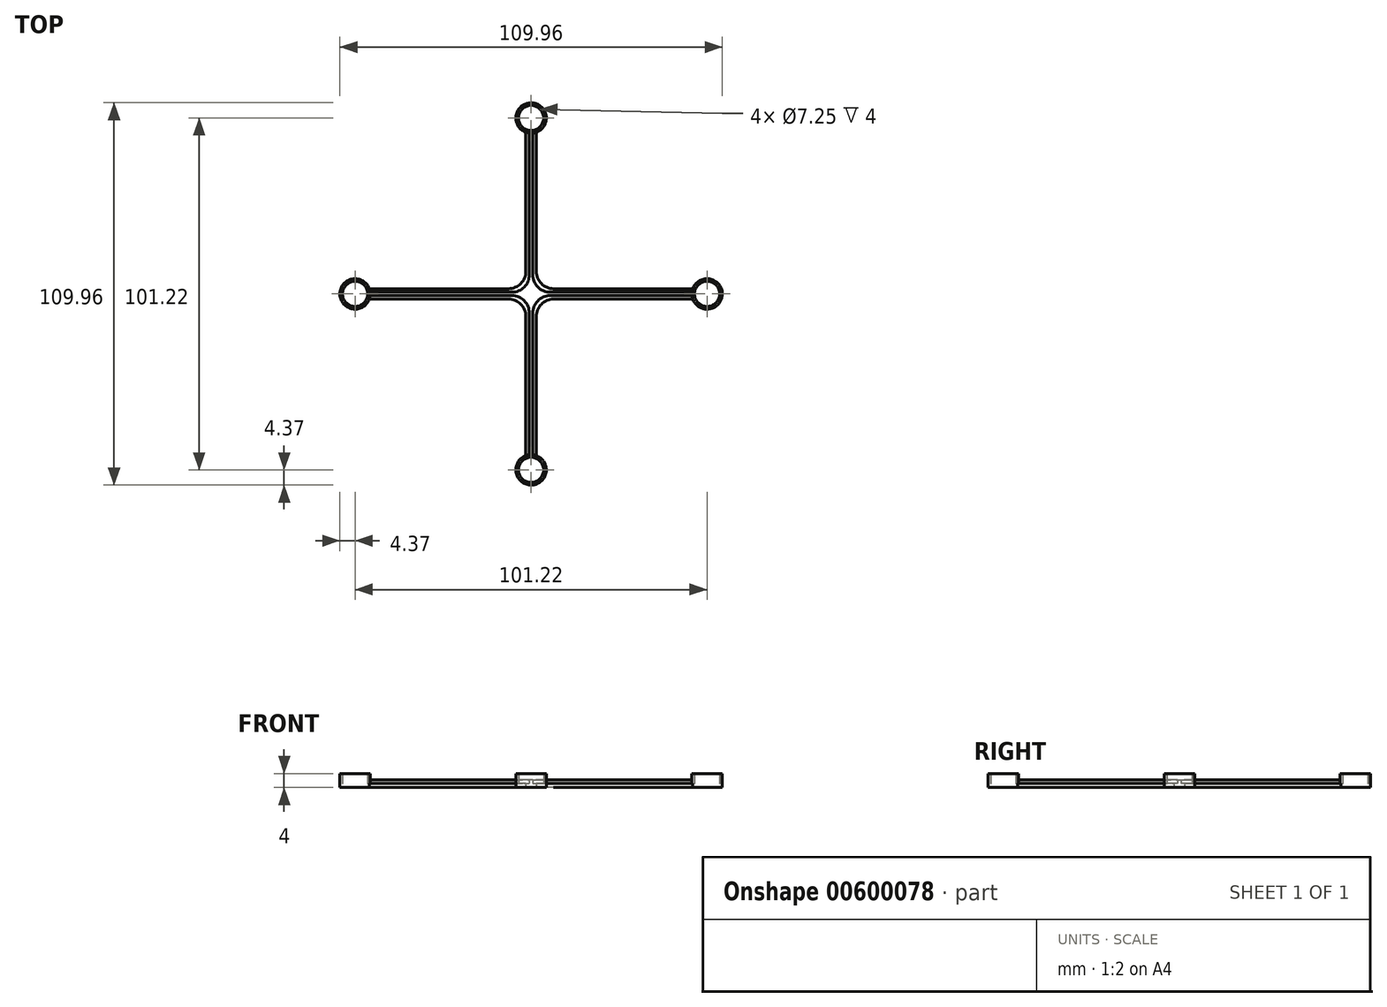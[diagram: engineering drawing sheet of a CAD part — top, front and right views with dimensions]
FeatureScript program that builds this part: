
annotation { "Feature Type Name" : "Feature", "Feature Type Description" : "" }
export const myFeature = defineFeature(function(context is Context, id is Id, definition is map)
    precondition{}
    {
        {
            var Q0;
            Q0=qCreatedBy(makeId("Top.planeOp"),FACE);
            var sketch = newSketch(context, id + "F0", { "sketchPlane" : qUnion([Q0])});
            skCircle(sketch, "E0", {"center": v(-50.6, 0) * mm, "radius": 3.62 * mm});
            skCircle(sketch, "E1", {"center": v(-50.6, 0) * mm, "radius": 4.38 * mm});
            skCircle(sketch, "E2.1.0", {"center": v(0, -50.6) * mm, "radius": 3.62 * mm});
            skCircle(sketch, "E2.1.1", {"center": v(0, -50.6) * mm, "radius": 4.38 * mm});
            skCircle(sketch, "E2.2.0", {"center": v(50.6, 0) * mm, "radius": 3.62 * mm});
            skCircle(sketch, "E2.2.1", {"center": v(50.6, 0) * mm, "radius": 4.38 * mm});
            skCircle(sketch, "E2.3.0", {"center": v(0, 50.6) * mm, "radius": 3.62 * mm});
            skCircle(sketch, "E2.3.1", {"center": v(0, 50.6) * mm, "radius": 4.38 * mm});
            skPoint(sketch, "E2.center", {"position": v(0, 0) * mm});
            skLineSegment(sketch, "E3", {"start": v(-46.5, 1.5) * mm, "end": v(-6.5, 1.5) * mm});
            skLineSegment(sketch, "E4", {"start": v(-1.5, 6.5) * mm, "end": v(-1.5, 46.5) * mm});
            skLineSegment(sketch, "E5.1.0", {"start": v(-6.5, -1.5) * mm, "end": v(-46.5, -1.5) * mm});
            skLineSegment(sketch, "E5.1.2", {"start": v(-1.5, -46.5) * mm, "end": v(-1.5, -6.5) * mm});
            skLineSegment(sketch, "E5.2.0", {"start": v(1.5, -6.5) * mm, "end": v(1.5, -46.5) * mm});
            skLineSegment(sketch, "E5.2.2", {"start": v(46.5, -1.5) * mm, "end": v(6.5, -1.5) * mm});
            skLineSegment(sketch, "E5.3.0", {"start": v(6.5, 1.5) * mm, "end": v(46.5, 1.5) * mm});
            skLineSegment(sketch, "E5.3.2", {"start": v(1.5, 46.5) * mm, "end": v(1.5, 6.5) * mm});
            skPoint(sketch, "E6.visualSharp", {"position": v(-1.5, -1.5) * mm});
            skArc(sketch, "E6.filletArc", {"start": v(-1.5, -6.5) * mm, "mid": v(-2.96, -2.96) * mm, "end": v(-6.5, -1.5) * mm});
            skPoint(sketch, "E7.visualSharp", {"position": v(-1.5, 1.5) * mm});
            skArc(sketch, "E7.filletArc", {"start": v(-6.5, 1.5) * mm, "mid": v(-2.96, 2.96) * mm, "end": v(-1.5, 6.5) * mm});
            skPoint(sketch, "E8.visualSharp", {"position": v(1.5, 1.5) * mm});
            skArc(sketch, "E8.filletArc", {"start": v(1.5, 6.5) * mm, "mid": v(2.96, 2.96) * mm, "end": v(6.5, 1.5) * mm});
            skPoint(sketch, "E9.visualSharp", {"position": v(1.5, -1.5) * mm});
            skArc(sketch, "E9.filletArc", {"start": v(6.5, -1.5) * mm, "mid": v(2.96, -2.96) * mm, "end": v(1.5, -6.5) * mm});
            skSolve(sketch);
        }
        {
            var Q0;
            Q0=qSketchRegion(id+"F0",true);
            var Q1;
            {var subQ3=sQuery(id+"F0.wireOp",EDGE,"E5.3.1");Q1=makeQuery(id+"F0.imprint","IMPRINT",FACE,{"disambiguationData":[TD([[makeQuery(id+"F0.imprint","IMPRINT",EDGE,{"derivedFrom":subQ3}),-1.0]])]});}
            var Q2;
            {var subQ3=sQuery(id+"F0.wireOp",EDGE,"112c20ca-e4e8-40d7-89ba-900f44e64bb5");Q2=makeQuery(id+"F0.imprint","IMPRINT",FACE,{"disambiguationData":[TD([[makeQuery(id+"F0.imprint","IMPRINT",EDGE,{"derivedFrom":subQ3}),-1.0]])]});}
            var Q3;
            {var subQ3=sQuery(id+"F0.wireOp",EDGE,"E5.1.1");Q3=makeQuery(id+"F0.imprint","IMPRINT",FACE,{"disambiguationData":[TD([[makeQuery(id+"F0.imprint","IMPRINT",EDGE,{"derivedFrom":subQ3}),-1.0]])]});}
            var Q4;
            {var subQ3=sQuery(id+"F0.wireOp",EDGE,"E5.2.1");Q4=makeQuery(id+"F0.imprint","IMPRINT",FACE,{"disambiguationData":[TD([[makeQuery(id+"F0.imprint","IMPRINT",EDGE,{"derivedFrom":subQ3}),-1.0]])]});}
            extrude(context, id + "F1", {"entities" : qUnion([Q0, Q1, Q2, Q3, Q4]), "depth" : 1.25 * mm});
        }
        {
            var Q0;
            Q0=makeQuery(id+"F1.opExtrude","CAP_FACE",FACE,{"disambiguationData":[OSD([sQuery(id+"F0.wireOp",EDGE,"E0"),sQuery(id+"F0.wireOp",EDGE,"E1"),sQuery(id+"F0.wireOp",EDGE,"E2.1.0"),sQuery(id+"F0.wireOp",EDGE,"E2.1.1"),sQuery(id+"F0.wireOp",EDGE,"E2.2.0"),sQuery(id+"F0.wireOp",EDGE,"E2.2.1"),sQuery(id+"F0.wireOp",EDGE,"E2.3.0"),sQuery(id+"F0.wireOp",EDGE,"E2.3.1"),sQuery(id+"F0.wireOp",EDGE,"E3"),sQuery(id+"F0.wireOp",EDGE,"E4"),sQuery(id+"F0.wireOp",EDGE,"E5.1.0"),sQuery(id+"F0.wireOp",EDGE,"E5.1.2"),sQuery(id+"F0.wireOp",EDGE,"E5.2.0"),sQuery(id+"F0.wireOp",EDGE,"E5.2.2"),sQuery(id+"F0.wireOp",EDGE,"E5.3.0"),sQuery(id+"F0.wireOp",EDGE,"E5.3.2"),sQuery(id+"F0.wireOp",EDGE,"E6.filletArc"),sQuery(id+"F0.wireOp",EDGE,"E7.filletArc"),sQuery(id+"F0.wireOp",EDGE,"E8.filletArc"),sQuery(id+"F0.wireOp",EDGE,"E9.filletArc")])],"isStart":false});
            var sketch = newSketch(context, id + "F2", { "sketchPlane" : qUnion([Q0])});
            skLineSegment(sketch, "E10.0", {"start": v(-5.5, 0.5) * mm, "end": v(-46.98, 0.5) * mm});
            skLineSegment(sketch, "E11.0.MirrorCS", {"start": v(-5.5, -0.5) * mm, "end": v(-46.98, -0.5) * mm});
            skLineSegment(sketch, "E12", {"start": v(-46.98, 0.5) * mm, "end": v(-46.98, -0.5) * mm});
            skLineSegment(sketch, "E13.1.0", {"start": v(-0.5, -46.98) * mm, "end": v(0.5, -46.98) * mm});
            skLineSegment(sketch, "E13.1.1", {"start": v(-0.5, -5.5) * mm, "end": v(-0.5, -46.98) * mm});
            skLineSegment(sketch, "E13.1.2", {"start": v(0.5, -5.5) * mm, "end": v(0.5, -46.98) * mm});
            skLineSegment(sketch, "E13.2.0", {"start": v(46.98, -0.5) * mm, "end": v(46.98, 0.5) * mm});
            skLineSegment(sketch, "E13.2.1", {"start": v(5.5, -0.5) * mm, "end": v(46.98, -0.5) * mm});
            skLineSegment(sketch, "E13.2.2", {"start": v(5.5, 0.5) * mm, "end": v(46.98, 0.5) * mm});
            skLineSegment(sketch, "E13.3.0", {"start": v(0.5, 46.98) * mm, "end": v(-0.5, 46.98) * mm});
            skLineSegment(sketch, "E13.3.1", {"start": v(0.5, 5.5) * mm, "end": v(0.5, 46.98) * mm});
            skLineSegment(sketch, "E13.3.2", {"start": v(-0.5, 5.5) * mm, "end": v(-0.5, 46.98) * mm});
            skPoint(sketch, "E13.center", {"position": v(0, 0) * mm});
            skPoint(sketch, "E14.orphan", {"position": v(-0.5, 0) * mm});
            skPoint(sketch, "E15.orphan", {"position": v(0, 0.5) * mm});
            skPoint(sketch, "E16.orphan", {"position": v(0.5, 0) * mm});
            skPoint(sketch, "E17.orphan", {"position": v(0, -0.5) * mm});
            skPoint(sketch, "E18.visualSharp", {"position": v(0.5, 0.5) * mm});
            skArc(sketch, "E18.filletArc", {"start": v(0.5, 5.5) * mm, "mid": v(1.96, 1.96) * mm, "end": v(5.5, 0.5) * mm});
            skPoint(sketch, "E19.visualSharp", {"position": v(0.5, -0.5) * mm});
            skArc(sketch, "E19.filletArc", {"start": v(5.5, -0.5) * mm, "mid": v(1.96, -1.96) * mm, "end": v(0.5, -5.5) * mm});
            skPoint(sketch, "E20.visualSharp", {"position": v(-0.5, -0.5) * mm});
            skArc(sketch, "E20.filletArc", {"start": v(-0.5, -5.5) * mm, "mid": v(-1.96, -1.96) * mm, "end": v(-5.5, -0.5) * mm});
            skPoint(sketch, "E21.visualSharp", {"position": v(-0.5, 0.5) * mm});
            skArc(sketch, "E21.filletArc", {"start": v(-5.5, 0.5) * mm, "mid": v(-1.96, 1.96) * mm, "end": v(-0.5, 5.5) * mm});
            skSolve(sketch);
        }
        {
            var Q0;
            Q0=qSketchRegion(id+"F2",true);
            extrude(context, id + "F3", {"entities" : qUnion([Q0]), "operationType" : NewBodyOperationType.ADD, "depth" : 1 * mm});
        }
        {
            var Q0;
            Q0=makeQuery(id+"F0.imprint","IMPRINT",FACE,{"disambiguationData":[TD([[makeQuery(id+"F0.imprint","IMPRINT",EDGE,{"derivedFrom":sQuery(id+"F0.wireOp",EDGE,"E2.2.0")}),-1.0]])]});
            var Q1;
            Q1=makeQuery(id+"F0.imprint","IMPRINT",FACE,{"disambiguationData":[TD([[makeQuery(id+"F0.imprint","IMPRINT",EDGE,{"derivedFrom":sQuery(id+"F0.wireOp",EDGE,"E2.1.0")}),-1.0]])]});
            var Q2;
            Q2=makeQuery(id+"F0.imprint","IMPRINT",FACE,{"disambiguationData":[TD([[makeQuery(id+"F0.imprint","IMPRINT",EDGE,{"derivedFrom":sQuery(id+"F0.wireOp",EDGE,"E0")}),-1.0]])]});
            var Q3;
            Q3=makeQuery(id+"F0.imprint","IMPRINT",FACE,{"disambiguationData":[TD([[makeQuery(id+"F0.imprint","IMPRINT",EDGE,{"derivedFrom":sQuery(id+"F0.wireOp",EDGE,"E2.3.0")}),-1.0]])]});
            extrude(context, id + "F4", {"entities" : qUnion([Q0, Q1, Q2, Q3]), "operationType" : NewBodyOperationType.ADD, "depth" : 4 * mm});
        }
    });
